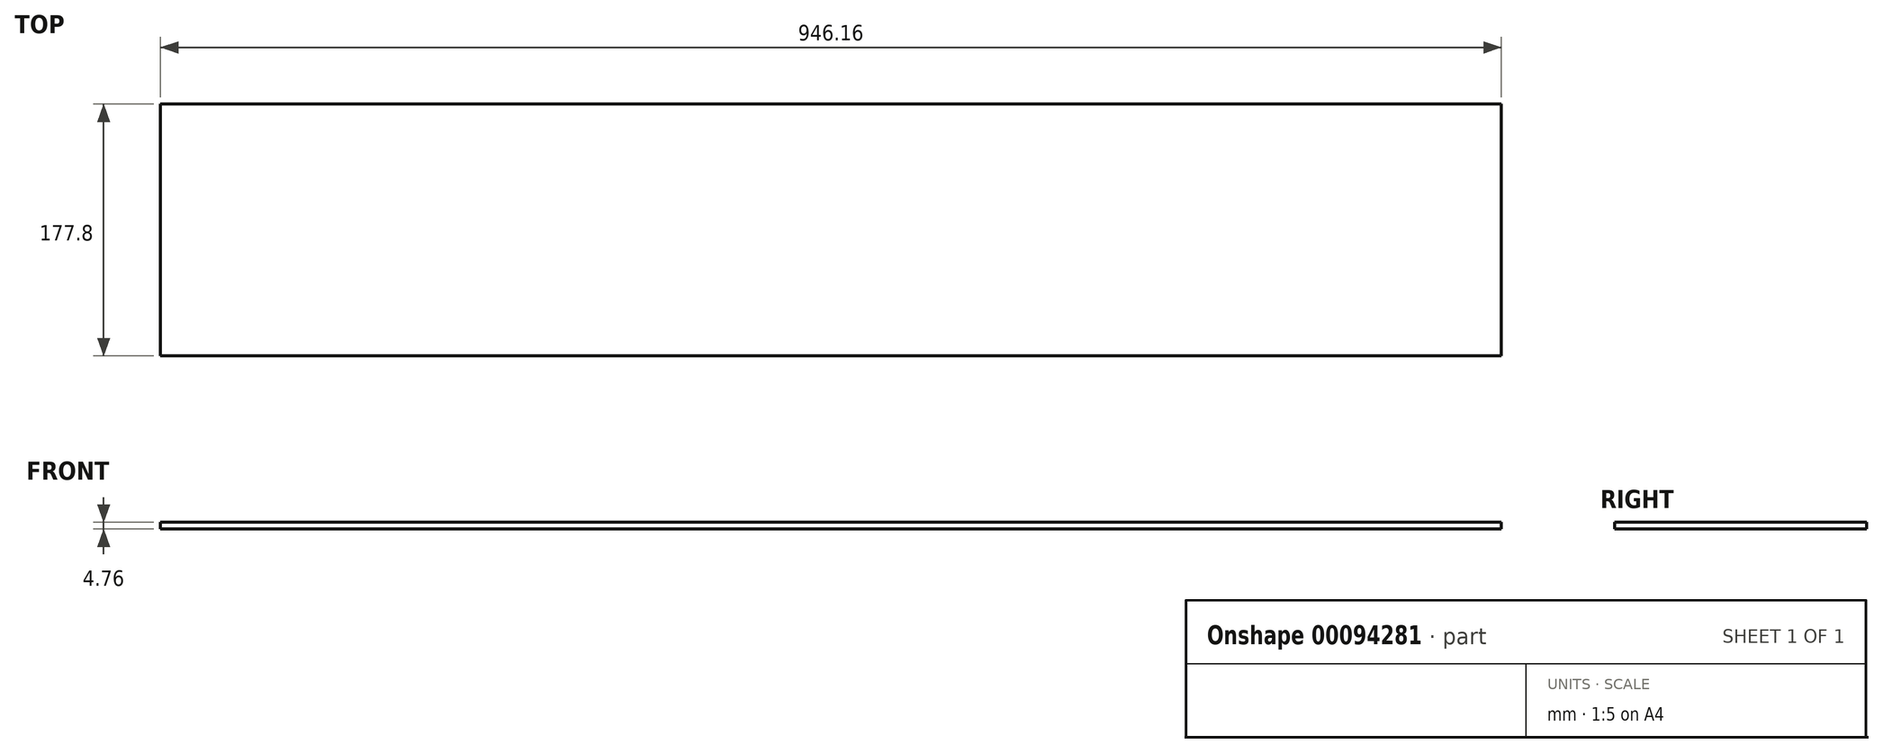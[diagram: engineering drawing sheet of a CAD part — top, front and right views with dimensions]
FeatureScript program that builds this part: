
annotation { "Feature Type Name" : "Feature", "Feature Type Description" : "" }
export const myFeature = defineFeature(function(context is Context, id is Id, definition is map)
    precondition{}
    {
        {
            var Q0;
            Q0=qCreatedBy(makeId("Top.planeOp"),FACE);
            var sketch = newSketch(context, id + "F0", { "sketchPlane" : qUnion([Q0])});
            skLineSegment(sketch, "E0.bottom", {"start": v(473.07, 88.9) * mm, "end": v(-473.08, 88.9) * mm});
            skLineSegment(sketch, "E0.top", {"start": v(473.08, -88.9) * mm, "end": v(-473.07, -88.9) * mm});
            skLineSegment(sketch, "E0.left", {"start": v(473.07, 88.9) * mm, "end": v(473.08, -88.9) * mm});
            skLineSegment(sketch, "E0.right", {"start": v(-473.08, 88.9) * mm, "end": v(-473.07, -88.9) * mm});
            skPoint(sketch, "E0.middle", {"position": v(0, 0) * mm});
            skSolve(sketch);
        }
        {
            var Q0;
            Q0 = qSketchRegion(id + "F0", true);
            extrude(context, id + "F1", {"entities" : qUnion([Q0]), "depth" : 4.76 * mm});
        }
    });
